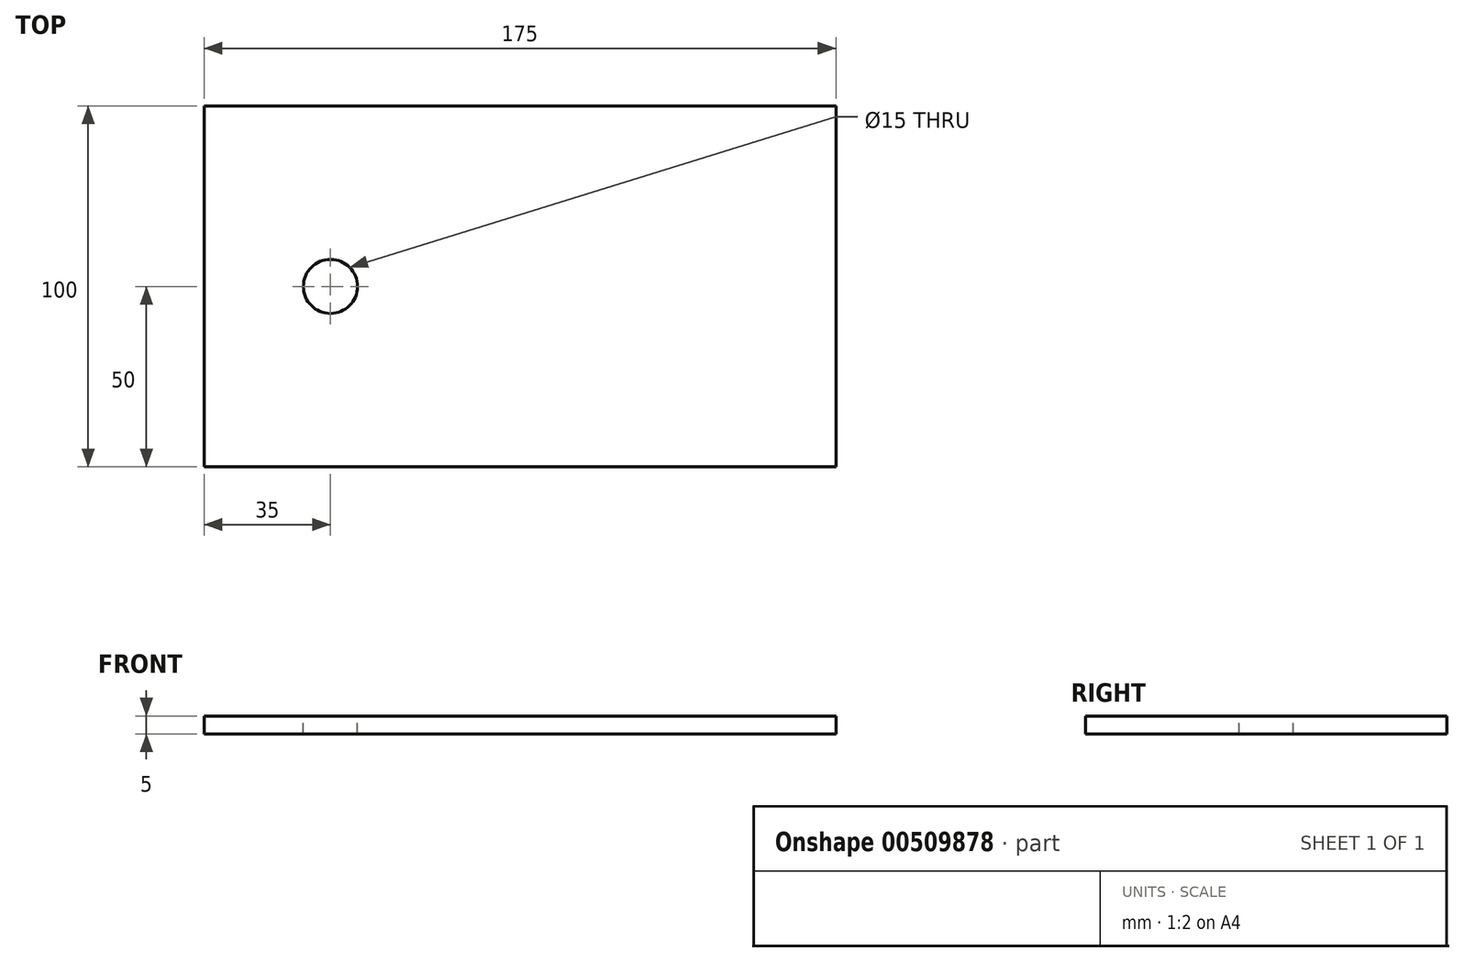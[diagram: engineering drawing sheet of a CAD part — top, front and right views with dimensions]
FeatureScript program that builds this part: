
annotation { "Feature Type Name" : "Feature", "Feature Type Description" : "" }
export const myFeature = defineFeature(function(context is Context, id is Id, definition is map)
    precondition{}
    {
        {
            var Q0;
            Q0=qCreatedBy(makeId("Top.planeOp"),FACE);
            var sketch = newSketch(context, id + "F0", { "sketchPlane" : qUnion([Q0])});
            skLineSegment(sketch, "E0.bottom", {"start": v(87.5, -50) * mm, "end": v(-87.5, -50) * mm});
            skLineSegment(sketch, "E0.top", {"start": v(87.5, 50) * mm, "end": v(-87.5, 50) * mm});
            skLineSegment(sketch, "E0.left", {"start": v(87.5, -50) * mm, "end": v(87.5, 50) * mm});
            skLineSegment(sketch, "E0.right", {"start": v(-87.5, -50) * mm, "end": v(-87.5, 50) * mm});
            skPoint(sketch, "E0.middle", {"position": v(0, 0) * mm});
            skSolve(sketch);
        }
        {
            var Q0;
            Q0=makeQuery(id+"F0.imprint","IMPRINT",FACE,{"disambiguationData":[TD([[makeQuery(id+"F0.imprint","IMPRINT",EDGE,{"derivedFrom":sQuery(id+"F0.wireOp",EDGE,"E0.bottom")}),-1.0]])]});
            extrude(context, id + "F1", {"entities" : qUnion([Q0]), "depth" : 5 * mm, "offsetDistance" : 25 * mm});
        }
        {
            var Q0;
            Q0=makeQuery(id+"F1.opExtrude","CAP_FACE",FACE,{"disambiguationData":[OSD([sQuery(id+"F0.wireOp",EDGE,"E0.bottom"),sQuery(id+"F0.wireOp",EDGE,"E0.top"),sQuery(id+"F0.wireOp",EDGE,"E0.left"),sQuery(id+"F0.wireOp",EDGE,"E0.right")])],"isStart":false});
            var sketch = newSketch(context, id + "F2", { "sketchPlane" : qUnion([Q0])});
            skCircle(sketch, "E1", {"center": v(-52.5, 0) * mm, "radius": 7.5 * mm});
            skSolve(sketch);
        }
        {
            var Q0;
            Q0=makeQuery(id+"F2.imprint","IMPRINT",FACE,{"disambiguationData":[TD([[makeQuery(id+"F2.imprint","IMPRINT",EDGE,{"derivedFrom":sQuery(id+"F2.wireOp",EDGE,"E1")}),1.0]])]});
            extrude(context, id + "F3", {"entities" : qUnion([Q0]), "operationType" : NewBodyOperationType.REMOVE, "oppositeDirection" : true, "depth" : 5 * mm, "offsetDistance" : 25 * mm});
        }
    });
